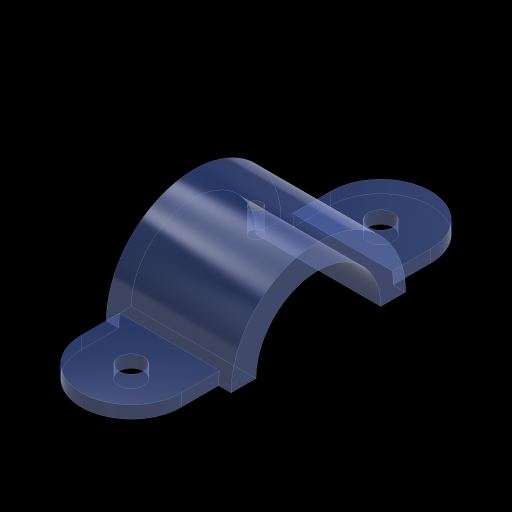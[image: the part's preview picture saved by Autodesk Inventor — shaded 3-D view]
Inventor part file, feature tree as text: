
AUTODESK INVENTOR PART (.ipt)
format: ipt  version: 2024 (Build 280153000, 153)  size: 162,816 bytes
history: native  units: in
note: dims shown in document units (in); Inventor stores cm internally (conversion verified against a paired STEP export)
features: extrude x4, sketch x3
ambient origin geometry x8: Origin, YZ Plane, XZ Plane, XY Plane, X Axis, Y Axis, Z Axis, Center Point
bodies: Solid1 (feature_tree)
feature tree (7):
  extrude  "BASE"  Depth=0.5in
  sketch  "Sketch2"  dims[d2=0.5in d3=1.0in]
  extrude  "REMOVED CENTER OF BASE"  Depth=1.0in
  extrude  "ARCH"  Depth=1.75in
  extrude  "TOPHOLE"  Depth=2.5in
  sketch  "Sketch1"  dims[d0=5.0in d1=0.5in]
  sketch  "Sketch3"  dims[d5=0.25in d6=0.0in d7=1.75in d8=1.25in d9=0.0in d10=0.0in d11=2.5in d12=0.0in d13=0.25in d14=0.0in d15=0.0in]
